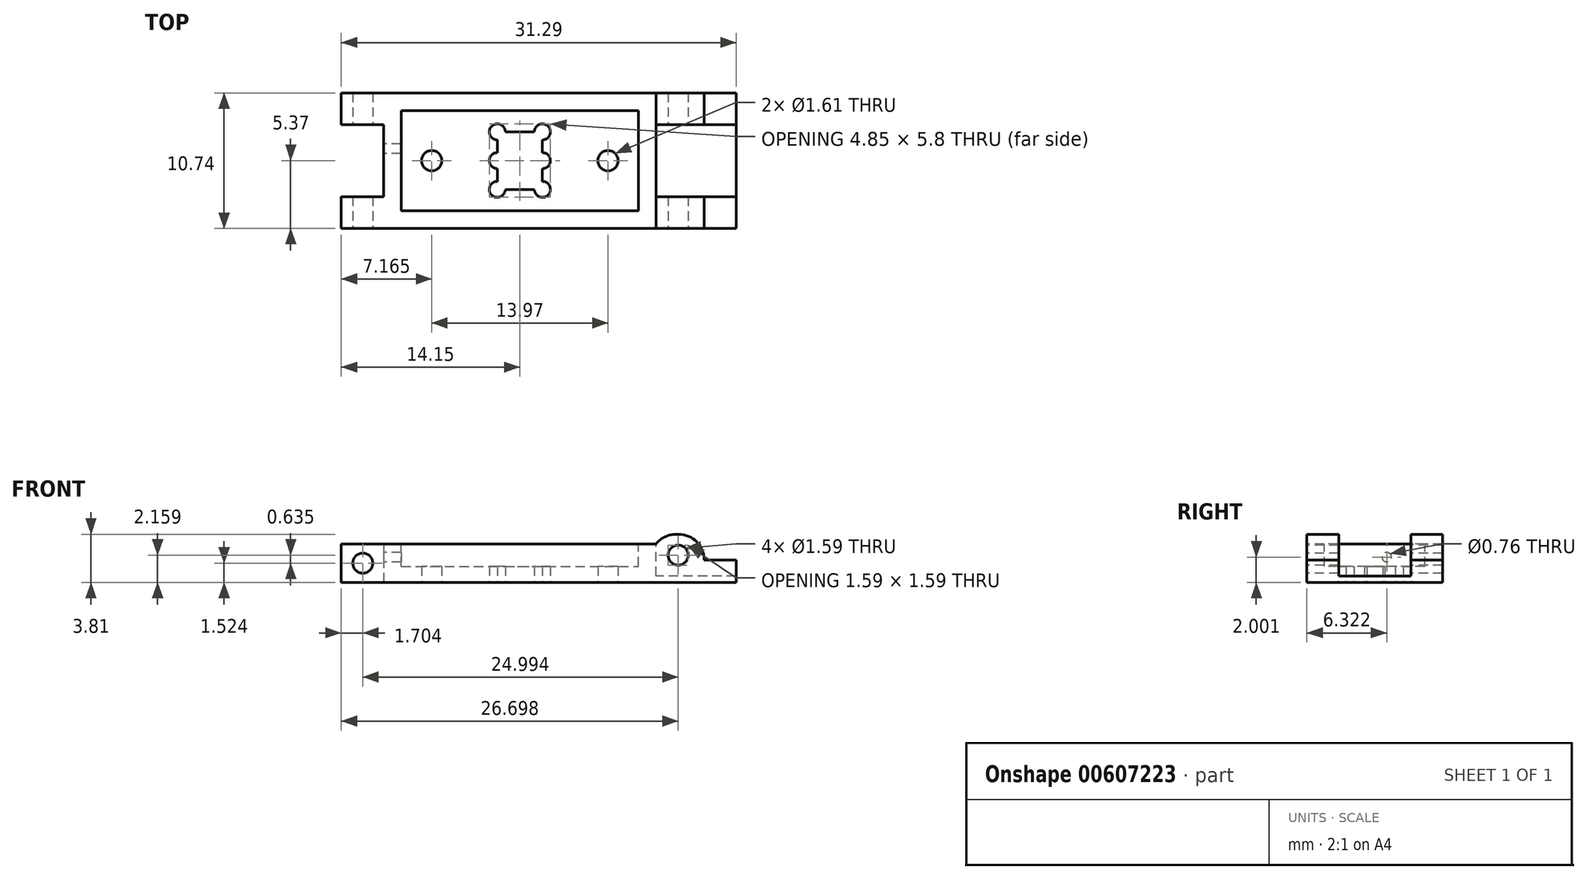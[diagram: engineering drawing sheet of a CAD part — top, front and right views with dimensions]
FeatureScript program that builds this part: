
annotation { "Feature Type Name" : "Feature", "Feature Type Description" : "" }
export const myFeature = defineFeature(function(context is Context, id is Id, definition is map)
    precondition{}
    {
        {
            var Q0;
            Q0=qCreatedBy(makeId("Top.planeOp"),FACE);
            var sketch = newSketch(context, id + "F0", { "sketchPlane" : qUnion([Q0])});
            skLineSegment(sketch, "E0.bottom", {"start": v(1.48, 1.88) * mm, "end": v(-1.47, 1.88) * mm, "construction": true});
            skLineSegment(sketch, "E0.top", {"start": v(1.48, -1.88) * mm, "end": v(-1.47, -1.88) * mm, "construction": true});
            skLineSegment(sketch, "E0.left", {"start": v(1.48, 1.88) * mm, "end": v(1.48, -1.88) * mm, "construction": true});
            skLineSegment(sketch, "E0.right", {"start": v(-1.47, 1.88) * mm, "end": v(-1.47, -1.88) * mm, "construction": true});
            skPoint(sketch, "E0.middle", {"position": v(0, 0) * mm});
            skLineSegment(sketch, "E1.bottom", {"start": v(1.79, 2.28) * mm, "end": v(-1.79, 2.28) * mm, "construction": true});
            skLineSegment(sketch, "E1.top", {"start": v(1.79, -2.28) * mm, "end": v(-1.79, -2.28) * mm, "construction": true});
            skLineSegment(sketch, "E2", {"start": v(-1.47, 1.88) * mm, "end": v(-1.79, 2.28) * mm, "construction": true});
            skLineSegment(sketch, "E3", {"start": v(1.79, -2.28) * mm, "end": v(1.48, -1.88) * mm, "construction": true});
            skLineSegment(sketch, "E4", {"start": v(-1.48, 1.88) * mm, "end": v(1.48, -1.88) * mm, "construction": true});
            skArc(sketch, "E5", {"start": v(-1.15, 2.28) * mm, "mid": v(-2.24, 2.73) * mm, "end": v(-1.79, 1.64) * mm});
            skArc(sketch, "E6", {"start": v(1.15, 2.28) * mm, "mid": v(2.24, 2.73) * mm, "end": v(1.79, 1.64) * mm});
            skArc(sketch, "E7", {"start": v(1.79, -1.64) * mm, "mid": v(2.24, -2.73) * mm, "end": v(1.15, -2.28) * mm});
            skArc(sketch, "E8", {"start": v(-1.15, -2.28) * mm, "mid": v(-2.24, -2.73) * mm, "end": v(-1.79, -1.64) * mm});
            skArc(sketch, "E9", {"start": v(-1.79, 0.64) * mm, "mid": v(-2.42, 0) * mm, "end": v(-1.79, -0.64) * mm});
            skArc(sketch, "E10", {"start": v(1.79, 0.64) * mm, "mid": v(2.42, 0) * mm, "end": v(1.79, -0.64) * mm});
            skLineSegment(sketch, "E11", {"start": v(-1.15, 2.28) * mm, "end": v(1.15, 2.28) * mm});
            skLineSegment(sketch, "E12", {"start": v(-1.79, 1.64) * mm, "end": v(-1.79, 0.64) * mm});
            skLineSegment(sketch, "E13", {"start": v(-1.79, -0.64) * mm, "end": v(-1.79, -1.64) * mm});
            skLineSegment(sketch, "E14", {"start": v(-1.15, -2.28) * mm, "end": v(1.15, -2.28) * mm});
            skLineSegment(sketch, "E15", {"start": v(1.79, -1.64) * mm, "end": v(1.79, -0.64) * mm});
            skLineSegment(sketch, "E16", {"start": v(1.79, 0.64) * mm, "end": v(1.79, 1.64) * mm});
            skLineSegment(sketch, "E17.bottom", {"start": v(-10.8, 5.37) * mm, "end": v(10.8, 5.37) * mm});
            skLineSegment(sketch, "E17.top", {"start": v(-10.8, -5.37) * mm, "end": v(10.8, -5.37) * mm});
            skLineSegment(sketch, "E17.left", {"start": v(-10.8, 5.37) * mm, "end": v(-10.8, -5.37) * mm});
            skLineSegment(sketch, "E18", {"start": v(-1.79, 2.28) * mm, "end": v(-1.79, -2.28) * mm, "construction": true});
            skLineSegment(sketch, "E19", {"start": v(1.79, 2.28) * mm, "end": v(1.79, -2.28) * mm, "construction": true});
            skLineSegment(sketch, "E20", {"start": v(10.8, 5.37) * mm, "end": v(17.15, 5.37) * mm});
            skLineSegment(sketch, "E21", {"start": v(17.15, 5.37) * mm, "end": v(17.15, -5.37) * mm});
            skLineSegment(sketch, "E22", {"start": v(17.15, -5.37) * mm, "end": v(10.8, -5.37) * mm});
            skCircle(sketch, "E23", {"center": v(-6.99, 0) * mm, "radius": 0.8 * mm});
            skCircle(sketch, "E24", {"center": v(6.99, 0) * mm, "radius": 0.8 * mm});
            skLineSegment(sketch, "E25.bottom", {"start": v(-10.8, 5.37) * mm, "end": v(-14.15, 5.37) * mm});
            skLineSegment(sketch, "E25.top", {"start": v(-10.8, 2.86) * mm, "end": v(-14.15, 2.86) * mm});
            skLineSegment(sketch, "E25.left", {"start": v(-10.8, 5.37) * mm, "end": v(-10.8, 2.86) * mm});
            skLineSegment(sketch, "E25.right", {"start": v(-14.15, 5.37) * mm, "end": v(-14.15, 2.86) * mm});
            skLineSegment(sketch, "E26.bottom", {"start": v(-10.8, -5.37) * mm, "end": v(-14.15, -5.37) * mm});
            skLineSegment(sketch, "E26.top", {"start": v(-10.8, -2.86) * mm, "end": v(-14.15, -2.86) * mm});
            skLineSegment(sketch, "E26.left", {"start": v(-10.8, -5.37) * mm, "end": v(-10.8, -2.86) * mm});
            skLineSegment(sketch, "E26.right", {"start": v(-14.15, -5.37) * mm, "end": v(-14.15, -2.86) * mm});
            skLineSegment(sketch, "E27", {"start": v(-6.99, 0) * mm, "end": v(6.99, 0) * mm, "construction": true});
            skSolve(sketch);
        }
        {
            var Q0;
            Q0=makeQuery(id+"F0.imprint","IMPRINT",FACE,{"disambiguationData":[TD([[makeQuery(id+"F0.imprint","IMPRINT",EDGE,{"derivedFrom":sQuery(id+"F0.wireOp",EDGE,"E25.bottom")}),1.0]])]});
            var Q1;
            Q1=makeQuery(id+"F0.imprint","IMPRINT",FACE,{"disambiguationData":[TD([[makeQuery(id+"F0.imprint","IMPRINT",EDGE,{"derivedFrom":sQuery(id+"F0.wireOp",EDGE,"E26.bottom")}),-1.0]])]});
            var Q2;
            Q2=makeQuery(id+"F0.imprint","IMPRINT",FACE,{"disambiguationData":[TD([[makeQuery(id+"F0.imprint","IMPRINT",EDGE,{"derivedFrom":sQuery(id+"F0.wireOp",EDGE,"E5")}),-1.0]])]});
            extrude(context, id + "F1", {"entities" : qUnion([Q0, Q1, Q2]), "depth" : 3.05 * mm, "offsetDistance" : 25.4 * mm});
        }
        {
            var Q0;
            Q0=makeQuery(id+"F1.opExtrude","CAP_FACE",FACE,{"disambiguationData":[OSD([sQuery(id+"F0.wireOp",EDGE,"E5"),sQuery(id+"F0.wireOp",EDGE,"E6"),sQuery(id+"F0.wireOp",EDGE,"E7"),sQuery(id+"F0.wireOp",EDGE,"E8"),sQuery(id+"F0.wireOp",EDGE,"E9"),sQuery(id+"F0.wireOp",EDGE,"E10"),sQuery(id+"F0.wireOp",EDGE,"E11"),sQuery(id+"F0.wireOp",EDGE,"E12"),sQuery(id+"F0.wireOp",EDGE,"E13"),sQuery(id+"F0.wireOp",EDGE,"E14"),sQuery(id+"F0.wireOp",EDGE,"E15"),sQuery(id+"F0.wireOp",EDGE,"E16"),sQuery(id+"F0.wireOp",EDGE,"E17.bottom"),sQuery(id+"F0.wireOp",EDGE,"E17.top"),sQuery(id+"F0.wireOp",EDGE,"E17.left"),sQuery(id+"F0.wireOp",EDGE,"E17.right")])],"isStart":false});
            var sketch = newSketch(context, id + "F2", { "sketchPlane" : qUnion([Q0])});
            skLineSegment(sketch, "E28.bottom", {"start": v(17.15, 5.37) * mm, "end": v(14.6, 5.37) * mm});
            skLineSegment(sketch, "E28.top", {"start": v(17.15, -5.37) * mm, "end": v(14.6, -5.37) * mm});
            skLineSegment(sketch, "E28.left", {"start": v(17.15, 5.37) * mm, "end": v(17.15, -5.37) * mm});
            skLineSegment(sketch, "E28.right", {"start": v(14.6, 5.37) * mm, "end": v(14.6, -5.37) * mm});
            skCircle(sketch, "E29", {"center": v(-6.99, 0) * mm, "radius": 1.47 * mm, "construction": true});
            skCircle(sketch, "E30", {"center": v(6.99, 0) * mm, "radius": 1.47 * mm, "construction": true});
            skLineSegment(sketch, "E31", {"start": v(-10.8, 0) * mm, "end": v(-9.4, 0) * mm, "construction": true});
            skLineSegment(sketch, "E32", {"start": v(0, -5.37) * mm, "end": v(0, -3.98) * mm, "construction": true});
            skLineSegment(sketch, "E33.bottom", {"start": v(-9.4, 3.98) * mm, "end": v(9.4, 3.98) * mm});
            skLineSegment(sketch, "E33.top", {"start": v(-9.4, -3.98) * mm, "end": v(9.4, -3.98) * mm});
            skLineSegment(sketch, "E33.left", {"start": v(-9.4, 3.98) * mm, "end": v(-9.4, -3.98) * mm});
            skLineSegment(sketch, "E33.right", {"start": v(9.4, 3.98) * mm, "end": v(9.4, -3.98) * mm});
            skPoint(sketch, "E33.middle", {"position": v(0, 0) * mm});
            skSolve(sketch);
        }
        {
            var Q0;
            Q0 = qSketchRegion(id + "F2", true);
            extrude(context, id + "F3", {"entities" : qUnion([Q0]), "operationType" : NewBodyOperationType.REMOVE, "oppositeDirection" : true, "depth" : 1.27 * mm, "offsetDistance" : 25.4 * mm});
        }
        {
            var Q0;
            Q0=makeQuery(id+"F1.opExtrude","CAP_FACE",FACE,{"disambiguationData":[OSD([sQuery(id+"F0.wireOp",EDGE,"E5"),sQuery(id+"F0.wireOp",EDGE,"E6"),sQuery(id+"F0.wireOp",EDGE,"E7"),sQuery(id+"F0.wireOp",EDGE,"E8"),sQuery(id+"F0.wireOp",EDGE,"E9"),sQuery(id+"F0.wireOp",EDGE,"E10"),sQuery(id+"F0.wireOp",EDGE,"E11"),sQuery(id+"F0.wireOp",EDGE,"E12"),sQuery(id+"F0.wireOp",EDGE,"E13"),sQuery(id+"F0.wireOp",EDGE,"E14"),sQuery(id+"F0.wireOp",EDGE,"E15"),sQuery(id+"F0.wireOp",EDGE,"E16"),sQuery(id+"F0.wireOp",EDGE,"E17.bottom"),sQuery(id+"F0.wireOp",EDGE,"E17.top"),sQuery(id+"F0.wireOp",EDGE,"E17.left"),sQuery(id+"F0.wireOp",EDGE,"E20"),sQuery(id+"F0.wireOp",EDGE,"E21"),sQuery(id+"F0.wireOp",EDGE,"E22"),sQuery(id+"F0.wireOp",EDGE,"E23"),sQuery(id+"F0.wireOp",EDGE,"E24"),sQuery(id+"F0.wireOp",EDGE,"E25.bottom"),sQuery(id+"F0.wireOp",EDGE,"E25.top"),sQuery(id+"F0.wireOp",EDGE,"E25.right"),sQuery(id+"F0.wireOp",EDGE,"E26.bottom"),sQuery(id+"F0.wireOp",EDGE,"E26.top"),sQuery(id+"F0.wireOp",EDGE,"E26.right")])],"isStart":false});
            var sketch = newSketch(context, id + "F4", { "sketchPlane" : qUnion([Q0])});
            skLineSegment(sketch, "E34.0", {"start": v(17.15, 5.37) * mm, "end": v(17.15, -5.37) * mm, "construction": true});
            skLineSegment(sketch, "E35.bottom", {"start": v(17.15, -2.86) * mm, "end": v(10.8, -2.86) * mm});
            skLineSegment(sketch, "E35.top", {"start": v(17.15, 2.86) * mm, "end": v(10.8, 2.86) * mm});
            skLineSegment(sketch, "E35.left", {"start": v(17.15, -2.86) * mm, "end": v(17.15, 2.86) * mm});
            skLineSegment(sketch, "E35.right", {"start": v(10.8, -2.86) * mm, "end": v(10.8, 2.86) * mm});
            skLineSegment(sketch, "E36", {"start": v(-10.8, 2.86) * mm, "end": v(10.8, 2.86) * mm, "construction": true});
            skLineSegment(sketch, "E37", {"start": v(10.8, -2.86) * mm, "end": v(-10.8, -2.86) * mm, "construction": true});
            skSolve(sketch);
        }
        {
            var Q0;
            Q0 = qSketchRegion(id + "F4", true);
            extrude(context, id + "F5", {"entities" : qUnion([Q0]), "operationType" : NewBodyOperationType.REMOVE, "oppositeDirection" : true, "depth" : 2.54 * mm, "offsetDistance" : 25.4 * mm});
        }
        {
            var Q0;
            Q0=makeQuery(id+"F1.opExtrude","SWEPT_FACE",FACE,{"disambiguationData":[OSD([sQuery(id+"F0.wireOp",EDGE,"E17.top"),sQuery(id+"F0.wireOp",EDGE,"E22"),sQuery(id+"F0.wireOp",EDGE,"E26.bottom")])]});
            var sketch = newSketch(context, id + "F6", { "sketchPlane" : qUnion([Q0])});
            skCircle(sketch, "E38", {"center": v(-12.45, 1.52) * mm, "radius": 0.8 * mm});
            skCircle(sketch, "E39", {"center": v(12.55, 2.16) * mm, "radius": 0.8 * mm});
            skLineSegment(sketch, "E40", {"start": v(-12.45, 3.05) * mm, "end": v(-12.45, 0) * mm, "construction": true});
            skLineSegment(sketch, "E41.0", {"start": v(14.6, 3.05) * mm, "end": v(10.8, 3.05) * mm, "construction": true});
            skSolve(sketch);
        }
        {
            var Q0;
            Q0 = qSketchRegion(id + "F6", true);
            extrude(context, id + "F7", {"entities" : qUnion([Q0]), "operationType" : NewBodyOperationType.REMOVE, "endBound" : BoundingType.THROUGH_ALL, "oppositeDirection" : true, "depth" : 25.4 * mm, "offsetDistance" : 25.4 * mm});
        }
        {
            var Q0;
            Q0=makeQuery(id+"F3.boolean.opBoolean","COPY",FACE,{"derivedFrom":makeQuery(id+"F3.opExtrude","CAP_FACE",FACE,{"disambiguationData":[OSD([sQuery(id+"F2.wireOp",EDGE,"E33.bottom"),sQuery(id+"F2.wireOp",EDGE,"E33.top"),sQuery(id+"F2.wireOp",EDGE,"E33.left"),sQuery(id+"F2.wireOp",EDGE,"E33.right")])],"isStart":false})});
            extrude(context, id + "F8", {"entities" : qUnion([Q0]), "operationType" : NewBodyOperationType.REMOVE, "oppositeDirection" : true, "depth" : 0.5 * mm, "offsetDistance" : 25.4 * mm});
        }
        {
            var Q0;
            Q0=makeQuery(id+"F1.opExtrude","CAP_FACE",FACE,{"disambiguationData":[OSD([sQuery(id+"F0.wireOp",EDGE,"E5"),sQuery(id+"F0.wireOp",EDGE,"E6"),sQuery(id+"F0.wireOp",EDGE,"E7"),sQuery(id+"F0.wireOp",EDGE,"E8"),sQuery(id+"F0.wireOp",EDGE,"E9"),sQuery(id+"F0.wireOp",EDGE,"E10"),sQuery(id+"F0.wireOp",EDGE,"E11"),sQuery(id+"F0.wireOp",EDGE,"E12"),sQuery(id+"F0.wireOp",EDGE,"E13"),sQuery(id+"F0.wireOp",EDGE,"E14"),sQuery(id+"F0.wireOp",EDGE,"E15"),sQuery(id+"F0.wireOp",EDGE,"E16"),sQuery(id+"F0.wireOp",EDGE,"E17.bottom"),sQuery(id+"F0.wireOp",EDGE,"E17.top"),sQuery(id+"F0.wireOp",EDGE,"E17.left"),sQuery(id+"F0.wireOp",EDGE,"E20"),sQuery(id+"F0.wireOp",EDGE,"E21"),sQuery(id+"F0.wireOp",EDGE,"E22"),sQuery(id+"F0.wireOp",EDGE,"E23"),sQuery(id+"F0.wireOp",EDGE,"E24"),sQuery(id+"F0.wireOp",EDGE,"E25.bottom"),sQuery(id+"F0.wireOp",EDGE,"E25.top"),sQuery(id+"F0.wireOp",EDGE,"E25.right"),sQuery(id+"F0.wireOp",EDGE,"E26.bottom"),sQuery(id+"F0.wireOp",EDGE,"E26.top"),sQuery(id+"F0.wireOp",EDGE,"E26.right")])],"isStart":false});
            var sketch = newSketch(context, id + "F9", { "sketchPlane" : qUnion([Q0])});
            skLineSegment(sketch, "E42.bottom", {"start": v(14.6, 5.37) * mm, "end": v(10.8, 5.37) * mm});
            skLineSegment(sketch, "E42.top", {"start": v(14.6, 2.86) * mm, "end": v(10.8, 2.86) * mm});
            skLineSegment(sketch, "E42.left", {"start": v(14.6, 5.37) * mm, "end": v(14.6, 2.86) * mm});
            skLineSegment(sketch, "E42.right", {"start": v(10.8, 5.37) * mm, "end": v(10.8, 2.86) * mm});
            skLineSegment(sketch, "E43.bottom", {"start": v(14.6, -2.86) * mm, "end": v(10.8, -2.86) * mm});
            skLineSegment(sketch, "E43.top", {"start": v(14.6, -5.37) * mm, "end": v(10.8, -5.37) * mm});
            skLineSegment(sketch, "E43.left", {"start": v(14.6, -2.86) * mm, "end": v(14.6, -5.37) * mm});
            skLineSegment(sketch, "E43.right", {"start": v(10.8, -2.86) * mm, "end": v(10.8, -5.37) * mm});
            skSolve(sketch);
        }
        {
            var Q0;
            Q0 = qSketchRegion(id + "F9", true);
            extrude(context, id + "F10", {"entities" : qUnion([Q0]), "operationType" : NewBodyOperationType.ADD, "depth" : 0.76 * mm, "offsetDistance" : 25.4 * mm});
        }
        {
            var Q0;
            Q0=makeQuery(id+"F10.opExtrude","CAP_EDGE",EDGE,{"disambiguationData":[OSD([sQuery(id+"F9.wireOp",EDGE,"E43.right")])],"isStart":false});
            var Q1;
            Q1=makeQuery(id+"F10.opExtrude","CAP_EDGE",EDGE,{"disambiguationData":[OSD([sQuery(id+"F9.wireOp",EDGE,"E42.right")])],"isStart":false});
            var Q2;
            Q2=makeQuery(id+"F10.opExtrude","CAP_EDGE",EDGE,{"disambiguationData":[OSD([sQuery(id+"F9.wireOp",EDGE,"E42.left")])],"isStart":false});
            var Q3;
            Q3=makeQuery(id+"F10.opExtrude","CAP_EDGE",EDGE,{"disambiguationData":[OSD([sQuery(id+"F9.wireOp",EDGE,"E43.left")])],"isStart":false});
            fillet(context, id + "F11", {"entities" : qUnion([Q0, Q1, Q2, Q3]), "radius" : 2.03 * mm, "tangentPropagation" : true, "allowEdgeOverflow" : false});
        }
        {
            var Q0;
            Q0=makeQuery(id+"F1.opExtrude","SWEPT_FACE",FACE,{"disambiguationData":[OSD([sQuery(id+"F0.wireOp",EDGE,"E17.left")])]});
            var sketch = newSketch(context, id + "F12", { "sketchPlane" : qUnion([Q0])});
            skCircle(sketch, "E44", {"center": v(-0.95, 2) * mm, "radius": 0.38 * mm});
            skSolve(sketch);
        }
        {
            var Q0;
            Q0 = qSketchRegion(id + "F12", true);
            var Q1;
            {var subQ0=sQuery(id+"F2.wireOp",EDGE,"E33.left");Q1=makeQuery(id+"F8.boolean.opBoolean","MERGE",FACE,{"derivedFrom":[makeQuery(id+"F3.boolean.opBoolean","COPY",FACE,{"derivedFrom":makeQuery(id+"F3.opExtrude","SWEPT_FACE",FACE,{"disambiguationData":[OSD([subQ0])]})}),makeQuery(id+"F8.opExtrude","SWEPT_FACE",FACE,{"disambiguationData":[OSD([subQ0])]})]});}
            extrude(context, id + "F13", {"entities" : qUnion([Q0, Q1]), "operationType" : NewBodyOperationType.REMOVE, "endBound" : BoundingType.UP_TO_NEXT, "oppositeDirection" : true, "depth" : 25.4 * mm, "offsetDistance" : 25.4 * mm});
        }
    });
